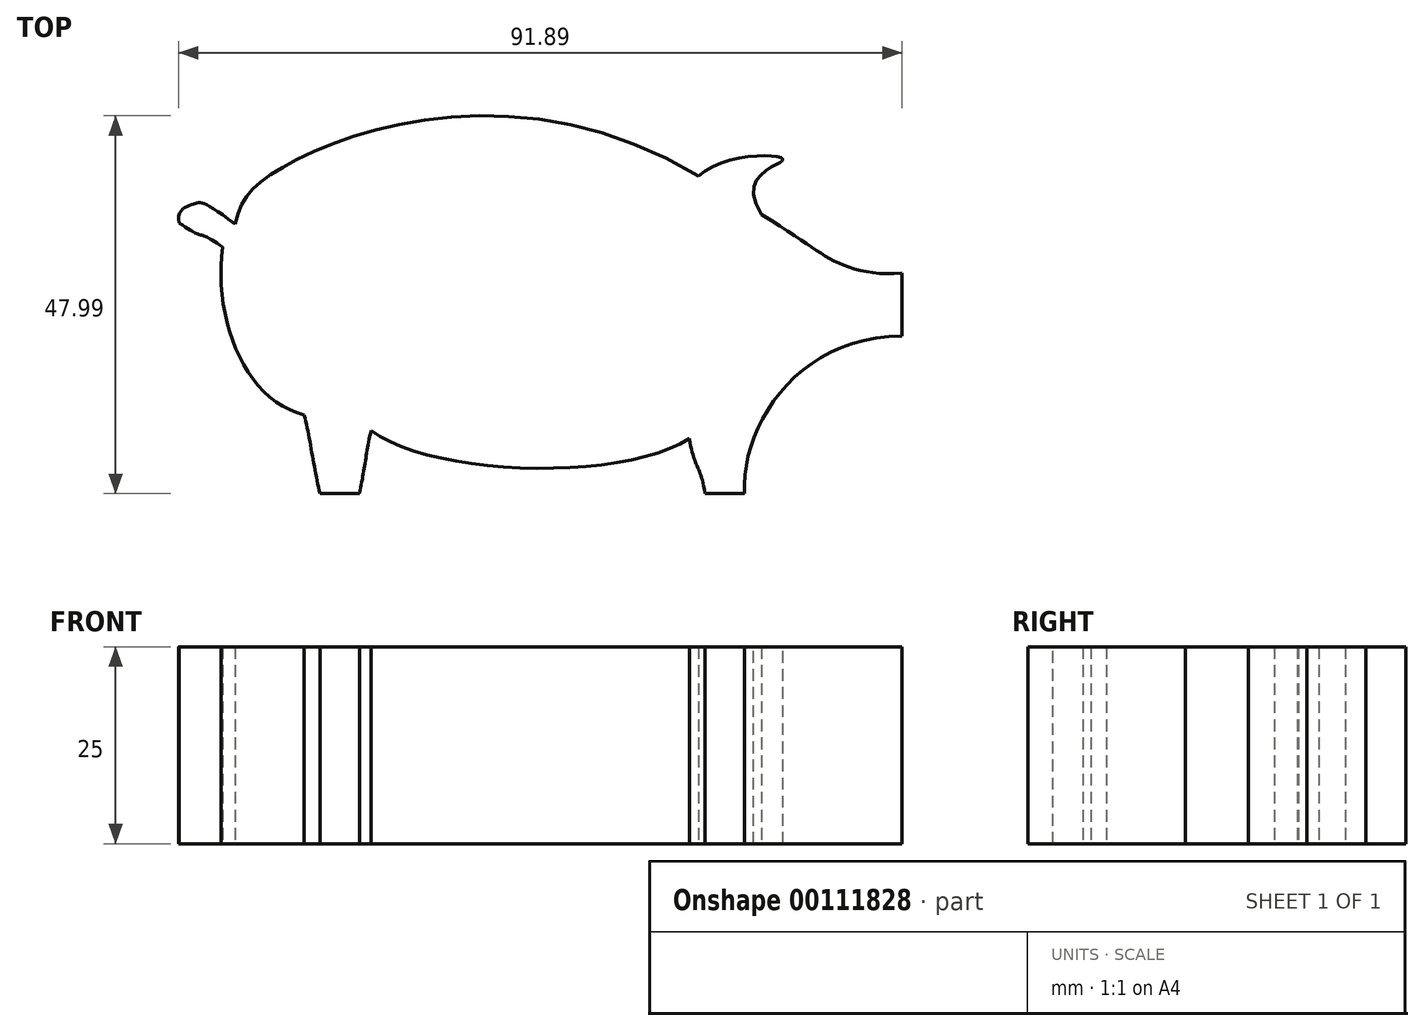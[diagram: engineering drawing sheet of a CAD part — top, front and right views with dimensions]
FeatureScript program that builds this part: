
annotation { "Feature Type Name" : "Feature", "Feature Type Description" : "" }
export const myFeature = defineFeature(function(context is Context, id is Id, definition is map)
    precondition{}
    {
        {
            var Q0;
            Q0=qCreatedBy(makeId("Top.planeOp"),FACE);
            var sketch = newSketch(context, id + "F0", { "sketchPlane" : qUnion([Q0])});
            skFitSpline(sketch, "E0", {"points": [v(14.17, 27.3) * mm, v(-39.33, 28.05) * mm, v(-44.73, 21.25) * mm], "startDerivative": vector(-95.62, 57.72) * mm, "endDerivative": vector(-7.97, -31.87) * mm});
            skFitSpline(sketch, "E1", {"points": [v(14.17, 27.3) * mm, v(24.87, 29.37) * mm, v(22.18, 22.46) * mm], "startDerivative": vector(17.32, 17.12) * mm, "endDerivative": vector(22.04, -34.16) * mm});
            skFitSpline(sketch, "E2", {"points": [v(22.18, 22.46) * mm, v(31.5, 16.5) * mm, v(40, 15) * mm], "startDerivative": vector(30.02, -18.65) * mm, "endDerivative": vector(23.34, 2.1) * mm});
            skFitSpline(sketch, "E3", {"points": [v(40, 7) * mm, v(20, -13) * mm], "startDerivative": vector(-39.05, 0) * mm, "endDerivative": vector(1.3, -26.44) * mm});
            skFitSpline(sketch, "E4", {"points": [v(15, -13) * mm, v(13, -6) * mm], "startDerivative": vector(-2.12, 12.07) * mm, "endDerivative": vector(-2.03, 12.3) * mm});
            skFitSpline(sketch, "E5", {"points": [v(13, -6) * mm, v(-27.42, -5) * mm], "startDerivative": vector(-25.08, -16.6) * mm, "endDerivative": vector(-23.32, 17.66) * mm});
            skFitSpline(sketch, "E6", {"points": [v(-27.42, -5) * mm, v(-28.92, -13) * mm], "startDerivative": vector(-2.05, -8.76) * mm, "endDerivative": vector(-2.05, -8.76) * mm});
            skFitSpline(sketch, "E7", {"points": [v(-33.92, -13) * mm, v(-35.92, -3) * mm], "startDerivative": vector(-2.24, 9.13) * mm, "endDerivative": vector(-2.24, 9.13) * mm});
            skFitSpline(sketch, "E8", {"points": [v(-44.73, 21.25) * mm, v(-50.15, 23.72) * mm, v(-51.8, 21.37) * mm], "startDerivative": vector(-21, 15.66) * mm, "endDerivative": vector(3.24, -12.07) * mm});
            skFitSpline(sketch, "E9", {"points": [v(-51.8, 21.37) * mm, v(-46.26, 18.3) * mm], "startDerivative": vector(9.7, -6.9) * mm, "endDerivative": vector(9.7, -6.9) * mm});
            skFitSpline(sketch, "E10", {"points": [v(-46.26, 18.3) * mm, v(-35.92, -3) * mm], "startDerivative": vector(-3.89, -27.2) * mm, "endDerivative": vector(22.49, -5.13) * mm});
            skLineSegment(sketch, "E11", {"start": v(-33.92, -13) * mm, "end": v(-28.92, -13) * mm});
            skLineSegment(sketch, "E12.trimOffspring", {"start": v(15, -13) * mm, "end": v(20, -13) * mm});
            skLineSegment(sketch, "E13", {"start": v(40, 15) * mm, "end": v(40, 7) * mm});
            skSolve(sketch);
        }
        {
            var Q0;
            Q0 = qSketchRegion(id + "F0", true);
            var Q1;
            Q1=makeQuery(id+"F0.imprint","IMPRINT",FACE,{"disambiguationData":[TD([[makeQuery(id+"F0.imprint","IMPRINT",EDGE,{"derivedFrom":sQuery(id+"F0.wireOp",EDGE,"E0")}),1.0]])]});
            extrude(context, id + "F1", {"entities" : qUnion([Q0, Q1]), "depth" : 25 * mm});
        }
    });
